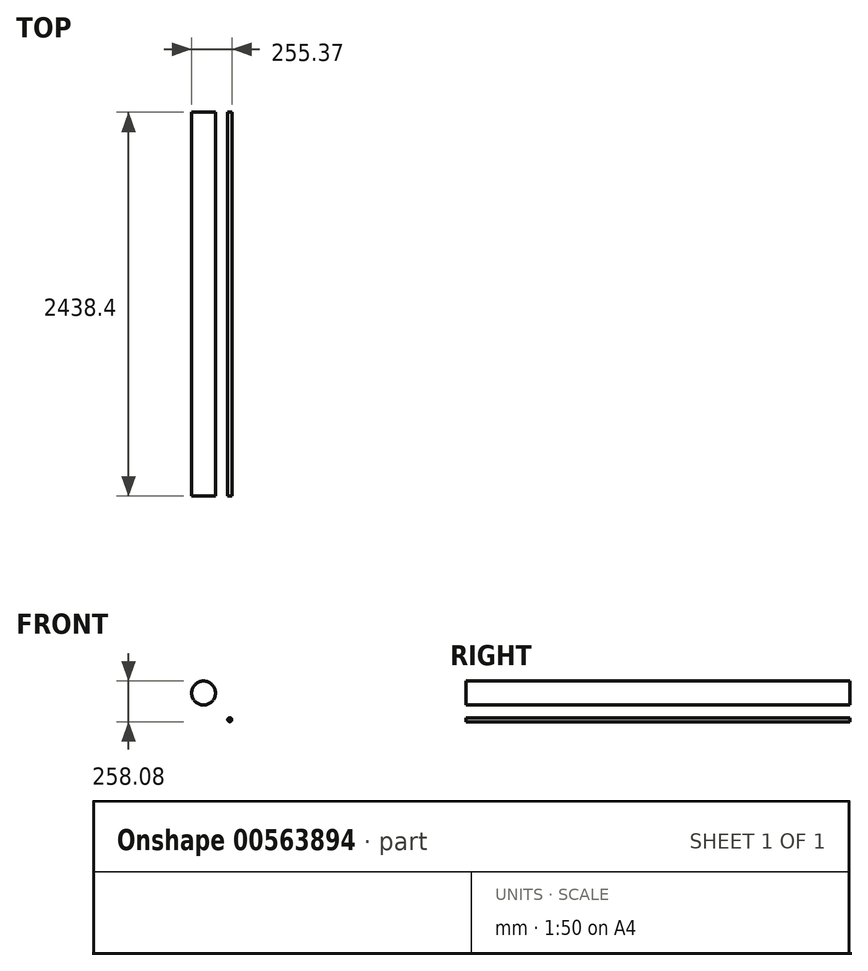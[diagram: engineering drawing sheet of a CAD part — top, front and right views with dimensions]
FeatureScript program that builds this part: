
annotation { "Feature Type Name" : "Feature", "Feature Type Description" : "" }
export const myFeature = defineFeature(function(context is Context, id is Id, definition is map)
    precondition{}
    {
        {
            var Q0;
            Q0=qCreatedBy(makeId("Front.planeOp"),FACE);
            var sketch = newSketch(context, id + "F0", { "sketchPlane" : qUnion([Q0])});
            skCircle(sketch, "E0", {"center": v(-132.19, 0) * mm, "radius": 12.78 * mm});
            skSolve(sketch);
        }
        {
            var Q0;
            Q0=makeQuery(id+"F0.imprint","IMPRINT",FACE,{"disambiguationData":[TD([[makeQuery(id+"F0.imprint","IMPRINT",EDGE,{"derivedFrom":sQuery(id+"F0.wireOp",EDGE,"E0")}),1.0]])]});
            extrude(context, id + "F1", {"entities" : qUnion([Q0]), "depth" : 2438.4 * mm, "offsetDistance" : 25.4 * mm});
        }
        {
            var Q0;
            Q0=qCreatedBy(makeId("Front.planeOp"),FACE);
            var sketch = newSketch(context, id + "F2", { "sketchPlane" : qUnion([Q0])});
            skCircle(sketch, "E1", {"center": v(-299.04, 169.56) * mm, "radius": 75.74 * mm});
            skSolve(sketch);
        }
        {
            var Q0;
            Q0=makeQuery(id+"F2.imprint","IMPRINT",FACE,{"disambiguationData":[TD([[makeQuery(id+"F2.imprint","IMPRINT",EDGE,{"derivedFrom":sQuery(id+"F2.wireOp",EDGE,"E1")}),1.0]])]});
            extrude(context, id + "F3", {"entities" : qUnion([Q0]), "depth" : 2438.4 * mm, "offsetDistance" : 25.4 * mm});
        }
    });
